# Revit family: oventrop_hycocon-vtz_1061704-16rfa
name_source: partatom
category: Арматура трубопроводов
revit_build: Autodesk Revit 2017 (Build: 20160225_1515(x64)
units: mm (PartAtom-declared; Revit-internal decimal feet)

## family parameters
Всегда вертикально = Да
Заголовок OmniClass = Adjusting/Controlling Valves for Liquid Services
На основе рабочей плоскости = Нет
Номер OmniClass = 23.65.55.14.17
Общий = Нет
При загрузке вырезать с полостями = Нет
Размер круглого соединителя = Использовать радиус
Тип детали = Клапан - Вставляется

## types (6) — shared parameters
Angle = 55.00°
Article Description = Brass balancing valve
Article Type = Hycocon VTZ 10617
Bonnet = Color RGB 35-35-35
Brass = Color RGB 168-128-48
Custom = Нет
EMCS Version = 2.0
ETIM Article Class = EC011463
Family Version = 10.14
IFCExportAs = IfcValveType
IFCExportType = PRESSUREREDUCING
Manufacturer URL = http://www.oventrop.de
Pressure Drop = 0.0 Па
Product Line = Oventrop
Rad3 = 13 мм
Rad4 = 15 мм
Rad4_a = 12.426 мм
Rad5 = 10 мм
Revit Version = 2015
Группа модели = Hycocon VTZ 10617
Изготовитель = Oventrop
Описание = Brass balancing valve

## per-type parameters (varying)
| type | Bonnet_width | D | Female_Port_Width | GTIN | H1 | H2 | Height | L1 | Length | Manufacturer Art. No. | NominalDiameter | Nut_Dimension | OuterDiameter | Rad1 | Rad2 | SW2 | URL | t2 |
| DN 15 | 38 мм | 21 мм | 13.2 мм | 4026755238235 | 19 мм | 27.032 мм | 77 мм | 28.295 мм | 80 мм | 1061704 | 12.700 мм | 27 мм | 21.3 мм | 10.5 мм | 13.5 мм | 31.177 мм | www.stabiplan.com | 2.64 мм |
| DN 20 | 38 мм | 26 мм | 14.5 мм | 4026755238242 | 21 мм | 30.556 мм | 79 мм | 33.693 мм | 82 мм | 1061706 | 19.050 мм | 32 мм | 26.9 мм | 13 мм | 16 мм | 36.95 мм | www.stabiplan.com | 2.9 мм |
| DN 25 | 38 мм | 33 мм | 16.8 мм | 4026755238259 | 23 мм | 36.899 мм | 81 мм | 39.09 мм | 92 мм | 1061708 | 25.400 мм | 41 мм | 33.7 мм | 16.5 мм | 20.5 мм | 47.343 мм | http://file-system.ru | 3.36 мм |
| DN 32 | 50 мм | 42 мм | 19.1 мм | 4026755250473 | 33 мм | 43.243 мм | 91 мм | 44.488 мм | 115 мм | 1061710 | 31.750 мм | 50 мм | 42.4 мм | 21 мм | 25 мм | 57.735 мм | www.stabiplan.com | 3.82 мм |
| DN 40 | 50 мм | 48 мм | 19.1 мм | 4026755250480 | 42 мм | 46.767 мм | 100 мм | 49.885 мм | 130 мм | 1061712 | 38.100 мм | 55 мм | 48.3 мм | 24 мм | 27.5 мм | 63.509 мм | www.stabiplan.com | 3.82 мм |
| DN 50 | 50 мм | 60 мм | 25.7 мм | 4026755364057 | 46 мм | 57.339 мм | 104 мм | 60.68 мм | 140 мм | 1061716 | 50.800 мм | 70 мм | 60.3 мм | 30 мм | 35 мм | 80.829 мм | www.stabiplan.com | 5.14 мм |

## geometry (parser evidence)
native form markers: Blend x4, Sweep x5
no freeform markers — native parametric forms only
